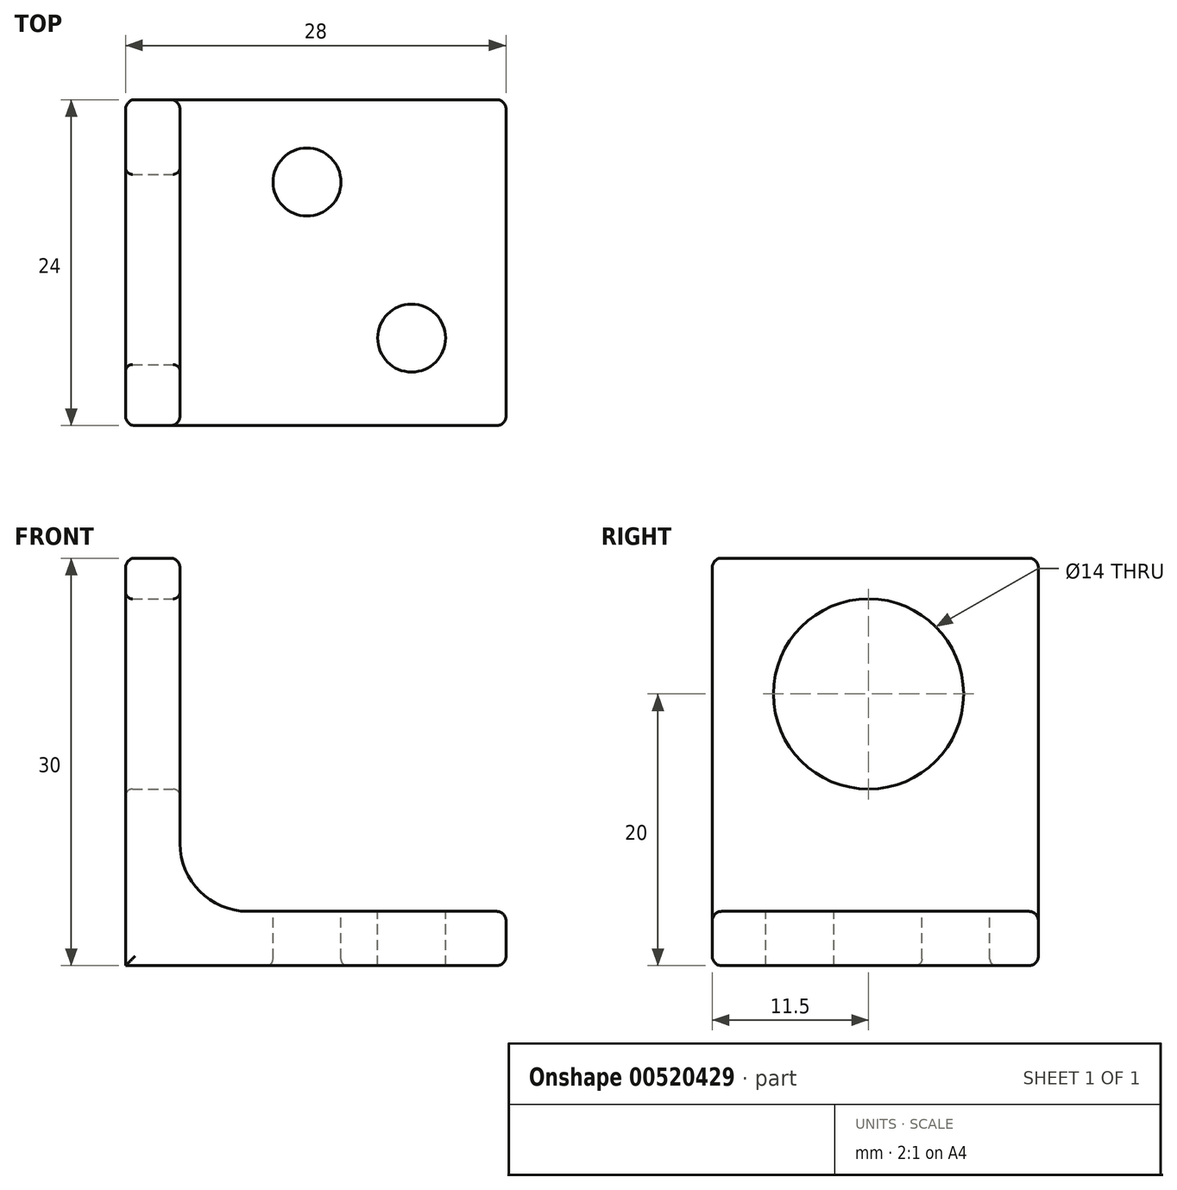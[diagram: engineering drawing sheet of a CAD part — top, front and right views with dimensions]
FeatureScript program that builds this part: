
annotation { "Feature Type Name" : "Feature", "Feature Type Description" : "" }
export const myFeature = defineFeature(function(context is Context, id is Id, definition is map)
    precondition{}
    {
        {
            var Q0;
            Q0=qCreatedBy(makeId("Front.planeOp"),FACE);
            var sketch = newSketch(context, id + "F0", { "sketchPlane" : qUnion([Q0])});
            skLineSegment(sketch, "E0", {"start": v(-24, 4) * mm, "end": v(-24, 30) * mm});
            skLineSegment(sketch, "E1.0", {"start": v(-28, 0) * mm, "end": v(-28, 30) * mm});
            skLineSegment(sketch, "E2.0", {"start": v(0, 4) * mm, "end": v(-24, 4) * mm});
            skLineSegment(sketch, "E3", {"start": v(-28, 30) * mm, "end": v(-24, 30) * mm});
            skLineSegment(sketch, "E4", {"start": v(0, 0) * mm, "end": v(0, 4) * mm});
            skLineSegment(sketch, "E5", {"start": v(-28, 0) * mm, "end": v(0, 0) * mm});
            skSolve(sketch);
        }
        {
            var Q0;
            Q0 = qSketchRegion(id + "F0", true);
            var Q1;
            Q1=makeQuery(id+"F0.imprint","IMPRINT",FACE,{"disambiguationData":[TD([[makeQuery(id+"F0.imprint","IMPRINT",EDGE,{"derivedFrom":sQuery(id+"F0.wireOp",EDGE,"E0")}),1.0]])]});
            extrude(context, id + "F1", {"entities" : qUnion([Q0, Q1]), "oppositeDirection" : true, "depth" : 24 * mm, "offsetDistance" : 25 * mm});
        }
        {
            var Q0;
            Q0=makeQuery(id+"F1.opExtrude","SWEPT_FACE",FACE,{"disambiguationData":[OSD([sQuery(id+"F0.wireOp",EDGE,"E2.0")])]});
            var sketch = newSketch(context, id + "F2", { "sketchPlane" : qUnion([Q0])});
            skCircle(sketch, "E6", {"center": v(-14.65, 17.93) * mm, "radius": 2.5 * mm});
            skCircle(sketch, "E7", {"center": v(-6.95, 6.45) * mm, "radius": 2.5 * mm});
            skSolve(sketch);
        }
        {
            var Q0;
            Q0 = qSketchRegion(id + "F2", true);
            extrude(context, id + "F3", {"entities" : qUnion([Q0]), "operationType" : NewBodyOperationType.REMOVE, "oppositeDirection" : true, "depth" : 25 * mm, "offsetDistance" : 25 * mm});
        }
        {
            var Q0;
            Q0=makeQuery(id+"F1.opExtrude","SWEPT_FACE",FACE,{"disambiguationData":[OSD([sQuery(id+"F0.wireOp",EDGE,"E0")])]});
            var sketch = newSketch(context, id + "F4", { "sketchPlane" : qUnion([Q0])});
            skCircle(sketch, "E8", {"center": v(11.5, 20) * mm, "radius": 7 * mm});
            skSolve(sketch);
        }
        {
            var Q0;
            Q0 = qSketchRegion(id + "F4", true);
            extrude(context, id + "F5", {"entities" : qUnion([Q0]), "operationType" : NewBodyOperationType.REMOVE, "oppositeDirection" : true, "depth" : 25 * mm, "offsetDistance" : 25 * mm});
        }
        {
            var Q0;
            Q0=makeQuery(id+"F1.opExtrude","SWEPT_EDGE",EDGE,{"disambiguationData":[OSD([sQuery(id+"F0.wireOp",EDGE,"E0"),sQuery(id+"F0.wireOp",EDGE,"E2.0")])]});
            fillet(context, id + "F6", {"entities" : qUnion([Q0]), "radius" : 5 * mm, "tangentPropagation" : true, "allowEdgeOverflow" : false});
        }
        {
            var Q0;
            Q0=makeQuery(id+"F1.opExtrude","SWEPT_FACE",FACE,{"disambiguationData":[OSD([sQuery(id+"F0.wireOp",EDGE,"E3")])]});
            var Q1;
            Q1=makeQuery(id+"F1.opExtrude","CAP_FACE",FACE,{"disambiguationData":[OSD([sQuery(id+"F0.wireOp",EDGE,"E0"),sQuery(id+"F0.wireOp",EDGE,"E1.0"),sQuery(id+"F0.wireOp",EDGE,"E2.0"),sQuery(id+"F0.wireOp",EDGE,"E3"),sQuery(id+"F0.wireOp",EDGE,"E4"),sQuery(id+"F0.wireOp",EDGE,"E5")])],"isStart":true});
            var Q2;
            Q2=makeQuery(id+"F1.opExtrude","SWEPT_FACE",FACE,{"disambiguationData":[OSD([sQuery(id+"F0.wireOp",EDGE,"E4")])]});
            var Q3;
            Q3=makeQuery(id+"F1.opExtrude","CAP_FACE",FACE,{"disambiguationData":[OSD([sQuery(id+"F0.wireOp",EDGE,"E0"),sQuery(id+"F0.wireOp",EDGE,"E1.0"),sQuery(id+"F0.wireOp",EDGE,"E2.0"),sQuery(id+"F0.wireOp",EDGE,"E3"),sQuery(id+"F0.wireOp",EDGE,"E4"),sQuery(id+"F0.wireOp",EDGE,"E5")])],"isStart":false});
            fillet(context, id + "F7", {"entities" : qUnion([Q0, Q1, Q2, Q3]), "radius" : .7 * mm, "tangentPropagation" : true, "allowEdgeOverflow" : false});
        }
        {
            var Q0;
            Q0=makeQuery(id+"F3.boolean.opBoolean","INTERSECT",EDGE,{"derivedFrom":[makeQuery(id+"F1.opExtrude","SWEPT_FACE",FACE,{"disambiguationData":[OSD([sQuery(id+"F0.wireOp",EDGE,"E5")])]}),makeQuery(id+"F3.opExtrude","SWEPT_FACE",FACE,{"disambiguationData":[OSD([sQuery(id+"F2.wireOp",EDGE,"E6")])]})]});
            var Q1;
            Q1=makeQuery(id+"F3.boolean.opBoolean","COPY",EDGE,{"derivedFrom":makeQuery(id+"F3.opExtrude","CAP_EDGE",EDGE,{"disambiguationData":[OSD([sQuery(id+"F2.wireOp",EDGE,"E7")])],"isStart":true})});
            var Q2;
            Q2=makeQuery(id+"F3.boolean.opBoolean","COPY",EDGE,{"derivedFrom":makeQuery(id+"F3.opExtrude","CAP_EDGE",EDGE,{"disambiguationData":[OSD([sQuery(id+"F2.wireOp",EDGE,"E6")])],"isStart":true})});
            var Q3;
            Q3=makeQuery(id+"F5.boolean.opBoolean","COPY",FACE,{"derivedFrom":makeQuery(id+"F5.opExtrude","SWEPT_FACE",FACE,{"disambiguationData":[OSD([sQuery(id+"F4.wireOp",EDGE,"E8")])]})});
            fillet(context, id + "F8", {"entities" : qUnion([Q0, Q1, Q2, Q3]), "radius" : .5 * mm, "tangentPropagation" : true, "allowEdgeOverflow" : false});
        }
    });
